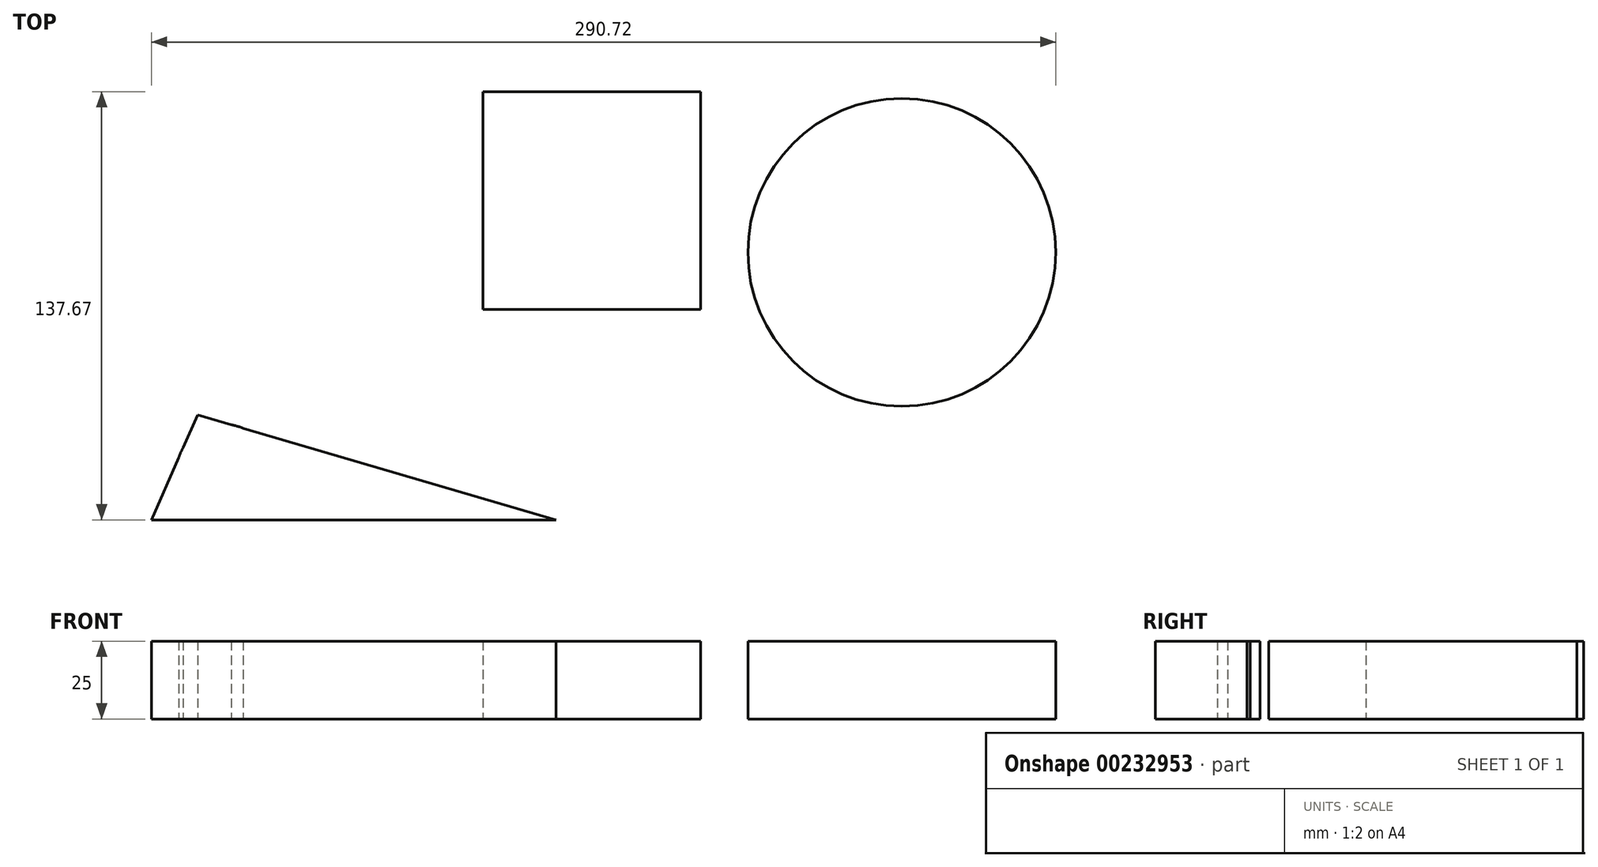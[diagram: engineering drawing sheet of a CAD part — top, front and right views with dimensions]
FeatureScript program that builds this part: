
annotation { "Feature Type Name" : "Feature", "Feature Type Description" : "" }
export const myFeature = defineFeature(function(context is Context, id is Id, definition is map)
    precondition{}
    {
        {
            var Q0;
            Q0=qCreatedBy(makeId("Top.planeOp"),FACE);
            var sketch = newSketch(context, id + "F0", { "sketchPlane" : qUnion([Q0])});
            skLineSegment(sketch, "E0.bottom", {"start": v(-69.72, 71.45) * mm, "end": v(0.28, 71.45) * mm});
            skLineSegment(sketch, "E0.top", {"start": v(-69.72, 1.45) * mm, "end": v(0.28, 1.45) * mm});
            skLineSegment(sketch, "E0.left", {"start": v(-69.72, 71.45) * mm, "end": v(-69.72, 1.45) * mm});
            skLineSegment(sketch, "E0.right", {"start": v(0.28, 71.45) * mm, "end": v(0.28, 1.45) * mm});
            skCircle(sketch, "E1", {"center": v(-34.72, 36.45) * mm, "radius": 34.67 * mm});
            skLineSegment(sketch, "E2.bottom", {"start": v(29.98, 54.77) * mm, "end": v(99.98, 54.77) * mm});
            skLineSegment(sketch, "E2.top", {"start": v(29.98, -15.23) * mm, "end": v(99.98, -15.23) * mm});
            skLineSegment(sketch, "E2.left", {"start": v(29.98, 54.77) * mm, "end": v(29.98, -15.23) * mm});
            skLineSegment(sketch, "E2.right", {"start": v(99.98, 54.77) * mm, "end": v(99.98, -15.23) * mm});
            skCircle(sketch, "E3", {"center": v(64.98, 19.77) * mm, "radius": 49.5 * mm});
            skLineSegment(sketch, "E4", {"start": v(-176.24, -66.22) * mm, "end": v(-46.24, -66.22) * mm});
            skLineSegment(sketch, "E5", {"start": v(-176.24, -66.22) * mm, "end": v(-161.4, -32.5) * mm});
            skLineSegment(sketch, "E6", {"start": v(-161.4, -32.5) * mm, "end": v(-46.24, -66.22) * mm});
            skCircle(sketch, "E7", {"center": v(-152.9, -50.73) * mm, "radius": 15.22 * mm});
            skPoint(sketch, "E7.first.point", {"position": v(-167.45, -46.26) * mm});
            skPoint(sketch, "E7.second.point", {"position": v(-138.52, -55.72) * mm});
            skPoint(sketch, "E7.third.point", {"position": v(-146.78, -36.79) * mm});
            skSolve(sketch);
        }
        {
            var Q0;
            Q0 = qSketchRegion(id + "F0", true);
            var Q1;
            Q1=makeQuery(id+"F0.imprint","IMPRINT",FACE,{"disambiguationData":[TD([[makeQuery(id+"F0.imprint","IMPRINT",EDGE,{"derivedFrom":sQuery(id+"F0.wireOp",EDGE,"E1")}),1.0]])]});
            extrude(context, id + "F1", {"entities" : qUnion([Q0, Q1]), "depth" : 25 * mm});
        }
    });
